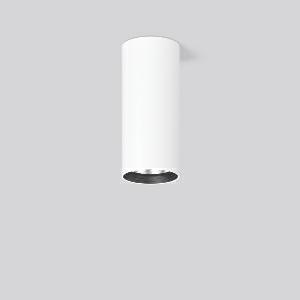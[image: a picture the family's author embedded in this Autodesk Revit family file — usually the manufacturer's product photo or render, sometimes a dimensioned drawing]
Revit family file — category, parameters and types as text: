
# Revit family: heledon_mini_a_931201_002_2_21ca
name_source: partatom
category: Lighting Fixtures
units: mm (PartAtom-declared; Revit-internal decimal feet)

## family parameters
Cut with Voids When Loaded = No
Host = Face
Light Source = No
Part Type = Normal
Room Calculation Point = No
Round Connector Dimension = Use Diameter
Shared = No

## types (1)
- HELEDON mini A (1 x LED Modul 927, 2300 lm, 2700)
    Apparent Load = 20 VA
    Approval mark = CE
    CIE Flux Codes = 99 100 100 100 100
    Color Rendering = 92
    Color Temperature = 2700
    Default Elevation = 1800 mm
    Description = Series: HELEDON mini
Cylindrical surface-mounted downlight. Housing: die-cast aluminium, powder-coated. Internal ceiling frame polycarbonate with bayonet mounting. Black plastic ring and recessed LED to prevent glare from the side. Optical assembly with reflector made of MIRO-Silver with 98% total light reflection for outstanding efficiency - can be changed without tools. Best colour rendering index Ra>90. Suitable for Ceiling mounting. Easy installation with a separate ceiling frame with bayonet mounting and plug connection. Driver integrated. Connected via plug-in connector. High quality converter without flickering and stroboscopic effect. The following accessories can be mounted without use of tools: interchangeable lenses, decorative glasses, honeycomb louvre, clear and frosted diffusers, white interchangeable plastic ring. 
Colour: traffic white, matt (RAL 9016)
Diameter: 87 mm
Height: 197 mm
Lamp: LED
Socket: without socket
Colour temperature: 2700K
Colour rendering index (CRI): 92
System power: 20 W
Rated luminous flux: 2300 lm
Luminous efficiency: 115 lm/W
Control gear: Regulated power supply
Protection class: I
Type of protection: IP 20
    Height = 197 mm
    Lamp = 1 x LED Modul 927
    Lamp Light Flux = 2300 lm
    Lamp count = 1
    Length = 87 mm
    Lifetime = 50000 h
    Luminous efficacy = 115 lm/W
    Manufacturer = RZB
    ModVariant = No
    Model = 931201.002.2
    Mounting Place = Ceiling
    Mounting Type = Surface mounted
    Number of Poles = 1
    OnlyDefault = Yes
    Power Factor = 1
    Product Name = HELEDON mini A
    Product group = Surface mounted downlights
    ProductGroupID = 302
    Protection Class = Protection class I
    Protection Degree = IP 20
    RLX_Detail_Level = 1
    RLX_Emergency_Light_Flux = 0 lm
    RLX_Emergency_Type = 0
    RLX_Emergency_Type_DB = No
    RlxData = <blob elided: 107233 chars, md5=df0f33b5>
    Socket = socket
    Standby Power = 0 W
    System Light Flux = 2300 lm
    System Power = 20 W
    Type Comments = Product without accessories
    Type Image = 931188.002.jpg
    URL = http://relux.com
    VarID = ---
    Voltage = 230 V
    Voltage Range = 220-240 V
    Weight = 0.00 kg
    Width = 0 mm  [stored 0 ft]

note: [stored X ft] marks values corroborated as IEEE doubles in the binary element streams (Revit-internal decimal feet)

## geometry (parser evidence)
native form markers: Blend x4, Sweep x9
no freeform markers — native parametric forms only
